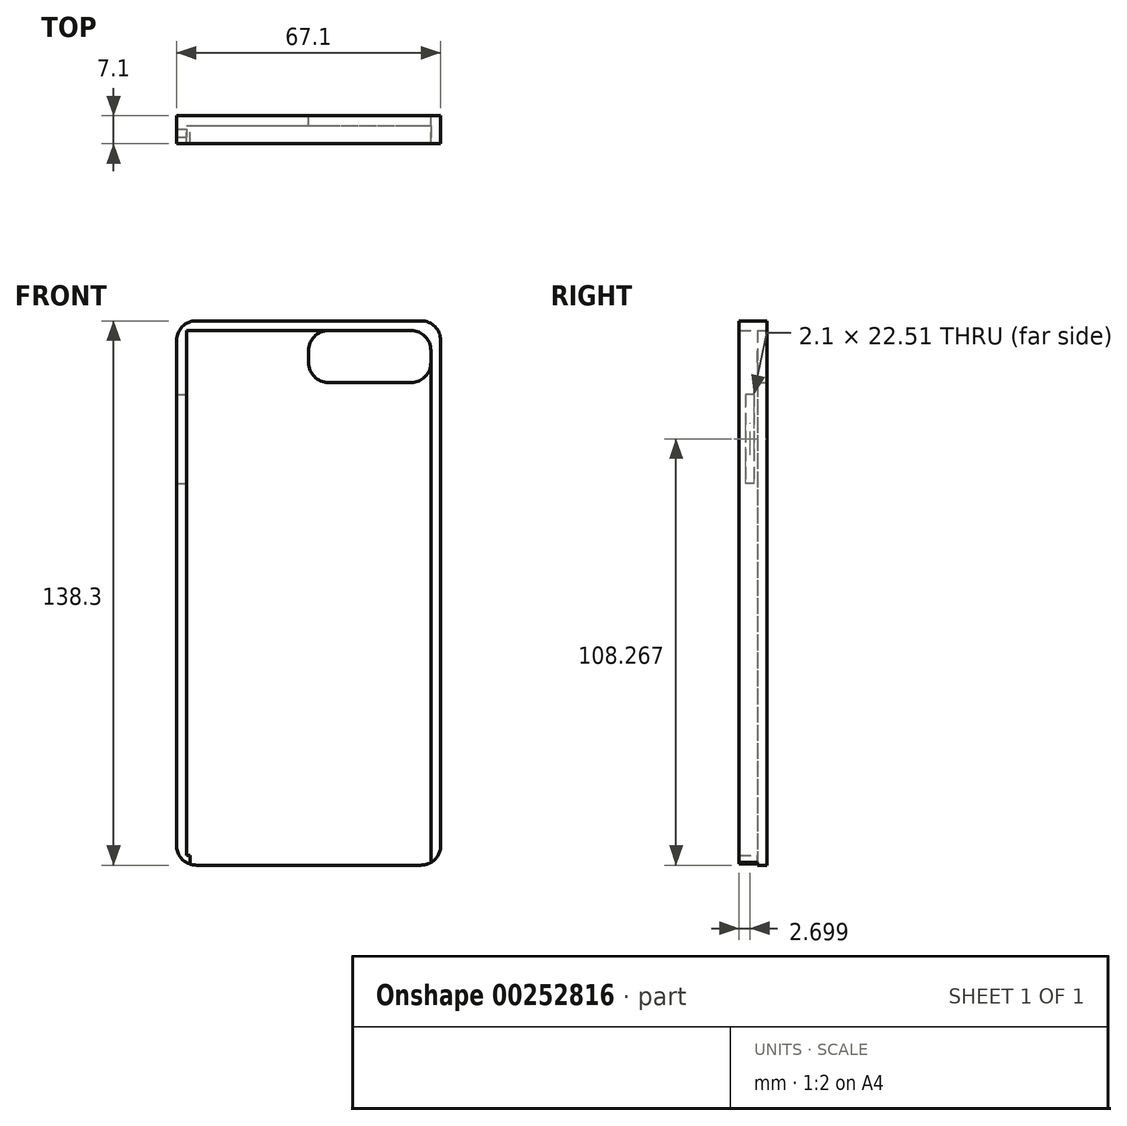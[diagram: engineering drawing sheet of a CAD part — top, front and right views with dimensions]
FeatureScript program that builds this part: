
annotation { "Feature Type Name" : "Feature", "Feature Type Description" : "" }
export const myFeature = defineFeature(function(context is Context, id is Id, definition is map)
    precondition{}
    {
        {
            var Q0;
            Q0=qCreatedBy(makeId("Front.planeOp"),FACE);
            var sketch = newSketch(context, id + "F0", { "sketchPlane" : qUnion([Q0])});
            skLineSegment(sketch, "E0.bottom", {"start": v(-33.55, 69.15) * mm, "end": v(33.55, 69.15) * mm});
            skLineSegment(sketch, "E0.top", {"start": v(-33.55, -69.15) * mm, "end": v(33.55, -69.15) * mm});
            skLineSegment(sketch, "E0.left", {"start": v(-33.55, 69.15) * mm, "end": v(-33.55, -69.15) * mm});
            skLineSegment(sketch, "E0.right", {"start": v(33.55, 69.15) * mm, "end": v(33.55, -69.15) * mm});
            skPoint(sketch, "E0.middle", {"position": v(0, 0) * mm});
            skSolve(sketch);
        }
        {
            var Q0;
            Q0=makeQuery(id+"F0.imprint","IMPRINT",FACE,{"disambiguationData":[TD([[makeQuery(id+"F0.imprint","IMPRINT",EDGE,{"derivedFrom":sQuery(id+"F0.wireOp",EDGE,"E0.bottom")}),-1.0]])]});
            extrude(context, id + "F1", {"entities" : qUnion([Q0]), "endBound" : BoundingType.SYMMETRIC, "depth" : 7.1 * mm});
        }
        {
            var Q0;
            Q0=makeQuery(id+"F1.opExtrude","CAP_FACE",FACE,{"disambiguationData":[OSD([sQuery(id+"F0.wireOp",EDGE,"E0.bottom"),sQuery(id+"F0.wireOp",EDGE,"E0.top"),sQuery(id+"F0.wireOp",EDGE,"E0.left"),sQuery(id+"F0.wireOp",EDGE,"E0.right")])],"isStart":false});
            shell(context, id + "F2", {"entities" : qUnion([Q0]), "thickness" : 2.5 * mm});
        }
        {
            var Q0;
            Q0=makeQuery(id+"F1.opExtrude","SWEPT_EDGE",EDGE,{"disambiguationData":[OSD([sQuery(id+"F0.wireOp",EDGE,"E0.bottom"),sQuery(id+"F0.wireOp",EDGE,"E0.left")])]});
            var Q1;
            Q1=makeQuery(id+"F1.opExtrude","SWEPT_EDGE",EDGE,{"disambiguationData":[OSD([sQuery(id+"F0.wireOp",EDGE,"E0.bottom"),sQuery(id+"F0.wireOp",EDGE,"E0.right")])]});
            var Q2;
            Q2=makeQuery(id+"F1.opExtrude","SWEPT_EDGE",EDGE,{"disambiguationData":[OSD([sQuery(id+"F0.wireOp",EDGE,"E0.top"),sQuery(id+"F0.wireOp",EDGE,"E0.right")])]});
            var Q3;
            Q3=makeQuery(id+"F1.opExtrude","SWEPT_EDGE",EDGE,{"disambiguationData":[OSD([sQuery(id+"F0.wireOp",EDGE,"E0.top"),sQuery(id+"F0.wireOp",EDGE,"E0.left")])]});
            fillet(context, id + "F3", {"entities" : qUnion([Q0, Q1, Q2, Q3]), "radius" : 5 * mm, "tangentPropagation" : true, "allowEdgeOverflow" : false});
        }
        {
            var Q0;
            Q0=makeQuery(id+"F2.opShell","OFFSET_FACE",FACE,{"disambiguationData":[OSD([sQuery(id+"F0.wireOp",EDGE,"E0.bottom"),sQuery(id+"F0.wireOp",EDGE,"E0.top"),sQuery(id+"F0.wireOp",EDGE,"E0.left"),sQuery(id+"F0.wireOp",EDGE,"E0.right")])]});
            var sketch = newSketch(context, id + "F4", { "sketchPlane" : qUnion([Q0])});
            skLineSegment(sketch, "E1.bottom", {"start": v(12.9, 60.39) * mm, "end": v(28.11, 60.39) * mm});
            skLineSegment(sketch, "E1.top", {"start": v(12.9, 53.5) * mm, "end": v(28.11, 53.5) * mm});
            skLineSegment(sketch, "E1.left", {"start": v(12.9, 60.39) * mm, "end": v(12.9, 53.5) * mm});
            skLineSegment(sketch, "E1.right", {"start": v(28.11, 60.39) * mm, "end": v(28.11, 53.5) * mm});
            skLineSegment(sketch, "E2.bottom", {"start": v(31.05, 66.65) * mm, "end": v(0, 66.65) * mm});
            skLineSegment(sketch, "E2.top", {"start": v(31.05, 53.5) * mm, "end": v(0, 53.5) * mm});
            skLineSegment(sketch, "E2.left", {"start": v(31.05, 66.65) * mm, "end": v(31.05, 53.5) * mm});
            skLineSegment(sketch, "E2.right", {"start": v(0, 66.65) * mm, "end": v(0, 53.5) * mm});
            skSolve(sketch);
        }
        {
            var Q0;
            Q0=makeQuery(id+"F4.imprint","IMPRINT",FACE,{"disambiguationData":[TD([[makeQuery(id+"F4.imprint","IMPRINT",EDGE,{"derivedFrom":sQuery(id+"F4.wireOp",EDGE,"E1.bottom")}),1.0]])]});
            var Q1;
            Q1=makeQuery(id+"F4.imprint","IMPRINT",FACE,{"disambiguationData":[TD([[makeQuery(id+"F4.imprint","IMPRINT",EDGE,{"derivedFrom":sQuery(id+"F4.wireOp",EDGE,"E1.bottom")}),-1.0]])]});
            extrude(context, id + "F5", {"entities" : qUnion([Q0, Q1]), "operationType" : NewBodyOperationType.REMOVE, "endBound" : BoundingType.SYMMETRIC, "depth" : 25 * mm});
        }
        {
            var Q0;
            Q0=makeQuery(id+"F2.opShell","OFFSET_FACE",FACE,{"disambiguationData":[OSD([sQuery(id+"F0.wireOp",EDGE,"E0.top")])]});
            var sketch = newSketch(context, id + "F6", { "sketchPlane" : qUnion([Q0])});
            skLineSegment(sketch, "E3.right", {"start": v(5.8, 1.53) * mm, "end": v(5.8, 0.95) * mm});
            skPoint(sketch, "E3.middle", {"position": v(0, 0) * mm});
            skLineSegment(sketch, "E4.bottom", {"start": v(-30.15, 1.05) * mm, "end": v(31.05, 1.05) * mm});
            skLineSegment(sketch, "E4.top", {"start": v(-30.15, -3.55) * mm, "end": v(31.05, -3.55) * mm});
            skLineSegment(sketch, "E4.left", {"start": v(-30.15, 1.05) * mm, "end": v(-30.15, -3.55) * mm});
            skLineSegment(sketch, "E4.right", {"start": v(31.05, 1.05) * mm, "end": v(31.05, -3.55) * mm});
            skLineSegment(sketch, "E5.top", {"start": v(-7.73, 0) * mm, "end": v(7.73, 0) * mm});
            skLineSegment(sketch, "E5.left", {"start": v(-7.73, -1.96) * mm, "end": v(-7.73, 0) * mm});
            skLineSegment(sketch, "E5.right", {"start": v(7.73, -1.96) * mm, "end": v(7.73, 0) * mm});
            skSolve(sketch);
        }
        {
            var Q0;
            Q0=makeQuery(id+"F5.boolean.opBoolean","COPY",EDGE,{"derivedFrom":makeQuery(id+"F5.opExtrude","SWEPT_EDGE",EDGE,{"disambiguationData":[OSD([sQuery(id+"F4.wireOp",EDGE,"E2.top"),sQuery(id+"F4.wireOp",EDGE,"E2.right")])]})});
            var Q1;
            Q1=makeQuery(id+"F5.boolean.opBoolean","COPY",EDGE,{"derivedFrom":makeQuery(id+"F5.opExtrude","SWEPT_EDGE",EDGE,{"disambiguationData":[OSD([sQuery(id+"F0.wireOp",EDGE,"E0.bottom"),sQuery(id+"F4.wireOp",EDGE,"E2.bottom"),sQuery(id+"F4.wireOp",EDGE,"E2.right")])]})});
            var Q2;
            Q2=makeQuery(id+"F5.boolean.opBoolean","MERGE",EDGE,{"derivedFrom":[makeQuery(id+"F2.opShell","OFFSET_EDGE",EDGE,{"disambiguationData":[OSD([sQuery(id+"F0.wireOp",EDGE,"E0.bottom"),sQuery(id+"F0.wireOp",EDGE,"E0.right")])]}),makeQuery(id+"F5.opExtrude","SWEPT_EDGE",EDGE,{"disambiguationData":[OSD([sQuery(id+"F4.wireOp",EDGE,"E2.bottom"),sQuery(id+"F4.wireOp",EDGE,"E2.left")])]})]});
            var Q3;
            Q3=makeQuery(id+"F5.boolean.opBoolean","COPY",EDGE,{"derivedFrom":makeQuery(id+"F5.opExtrude","SWEPT_EDGE",EDGE,{"disambiguationData":[OSD([sQuery(id+"F0.wireOp",EDGE,"E0.right"),sQuery(id+"F4.wireOp",EDGE,"E2.top"),sQuery(id+"F4.wireOp",EDGE,"E2.left")])]})});
            fillet(context, id + "F7", {"entities" : qUnion([Q0, Q1, Q2, Q3]), "radius" : 5 * mm, "tangentPropagation" : true, "allowEdgeOverflow" : false});
        }
        {
            var Q0;
            Q0 = qSketchRegion(id + "F6", true);
            extrude(context, id + "F8", {"entities" : qUnion([Q0]), "operationType" : NewBodyOperationType.REMOVE, "oppositeDirection" : true, "depth" : 25 * mm});
        }
        {
            var Q0;
            Q0=makeQuery(id+"F1.opExtrude","SWEPT_FACE",FACE,{"disambiguationData":[OSD([sQuery(id+"F0.wireOp",EDGE,"E0.left")])]});
            var sketch = newSketch(context, id + "F9", { "sketchPlane" : qUnion([Q0])});
            skLineSegment(sketch, "E6.bottom", {"start": v(-0.2, 50.37) * mm, "end": v(1.9, 50.37) * mm});
            skLineSegment(sketch, "E6.top", {"start": v(-0.2, 27.86) * mm, "end": v(1.9, 27.86) * mm});
            skLineSegment(sketch, "E6.left", {"start": v(-0.2, 50.37) * mm, "end": v(-0.2, 27.86) * mm});
            skLineSegment(sketch, "E6.right", {"start": v(1.9, 50.37) * mm, "end": v(1.9, 27.86) * mm});
            skSolve(sketch);
        }
        {
            var Q0;
            Q0=makeQuery(id+"F9.imprint","IMPRINT",FACE,{"disambiguationData":[TD([[makeQuery(id+"F9.imprint","IMPRINT",EDGE,{"derivedFrom":sQuery(id+"F9.wireOp",EDGE,"E6.bottom")}),-1.0]])]});
            extrude(context, id + "F10", {"entities" : qUnion([Q0]), "operationType" : NewBodyOperationType.REMOVE, "endBound" : BoundingType.SYMMETRIC, "depth" : 25 * mm});
        }
    });
